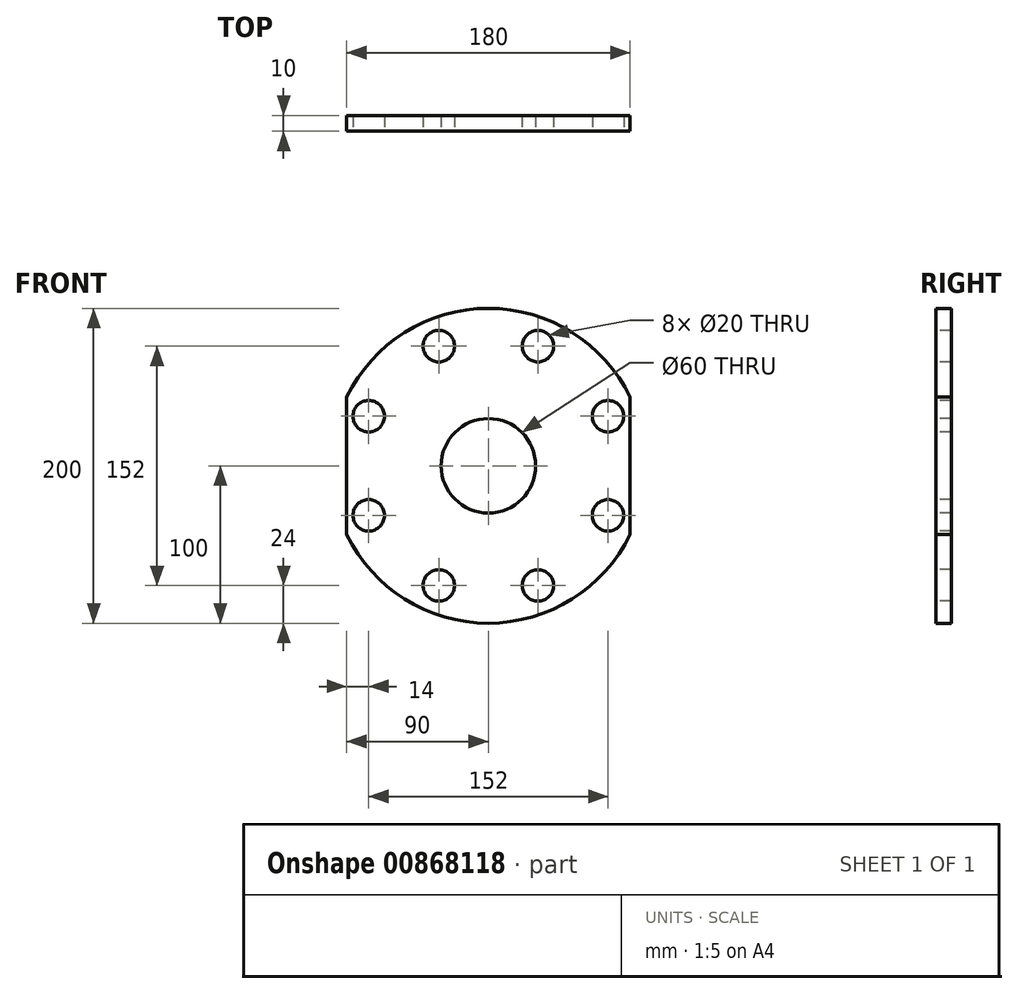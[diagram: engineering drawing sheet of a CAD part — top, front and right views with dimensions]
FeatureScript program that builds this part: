
annotation { "Feature Type Name" : "Feature", "Feature Type Description" : "" }
export const myFeature = defineFeature(function(context is Context, id is Id, definition is map)
    precondition{}
    {
        {
            var Q0;
            Q0=qCreatedBy(makeId("Front.planeOp"),FACE);
            var sketch = newSketch(context, id + "F0", { "sketchPlane" : qUnion([Q0])});
            skCircle(sketch, "E0", {"center": v(0, 0) * mm, "radius": 100 * mm});
            skSolve(sketch);
        }
        {
            var Q0;
            Q0=makeQuery(id+"F0.imprint","IMPRINT",FACE,{"disambiguationData":[TD([[makeQuery(id+"F0.imprint","IMPRINT",EDGE,{"derivedFrom":sQuery(id+"F0.wireOp",EDGE,"E0")}),1.0]])]});
            var sketch = newSketch(context, id + "F1", { "sketchPlane" : qUnion([Q0])});
            skLineSegment(sketch, "E1.bottom", {"start": v(90, 100) * mm, "end": v(-90, 100) * mm});
            skLineSegment(sketch, "E1.top", {"start": v(90, -100) * mm, "end": v(-90, -100) * mm});
            skLineSegment(sketch, "E1.left", {"start": v(90, 100) * mm, "end": v(90, -100) * mm});
            skLineSegment(sketch, "E1.right", {"start": v(-90, 100) * mm, "end": v(-90, -100) * mm});
            skPoint(sketch, "E1.middle", {"position": v(0, 0) * mm});
            skSolve(sketch);
        }
        {
            var Q0;
            Q0 = qSketchRegion(id + "F0", true);
            extrude(context, id + "F2", {"entities" : qUnion([Q0]), "depth" : 10 * mm, "offsetDistance" : 25 * mm});
        }
        {
            var Q0;
            {var subQ0=sQuery(id+"F1.wireOp",EDGE,"E1.right");var subQ1=sQuery(id+"F1.wireOp",EDGE,"E1.bottom");var subQ2=makeQuery(id+"F1.imprint","INTERSECT",VERTEX,{"derivedFrom":[subQ1,subQ0]});Q0=makeQuery(id+"F1.imprint","IMPRINT",FACE,{"disambiguationData":[TD([[makeQuery(id+"F1.imprint","IMPRINT",EDGE,{"disambiguationData":[TD([[subQ2,1.0]])],"derivedFrom":subQ1}),1.0]])]});}
            var Q1;
            {var subQ0=sQuery(id+"F1.wireOp",EDGE,"E1.right");var subQ1=makeQuery(id+"F0.imprint","IMPRINT",EDGE,{"derivedFrom":sQuery(id+"F0.wireOp",EDGE,"E0")});var subQ2=makeQuery(id+"F1.imprint","INTERSECT",VERTEX,{"disambiguationData":[OD(0.0)],"derivedFrom":[subQ1,subQ0]});Q1=makeQuery(id+"F1.imprint","IMPRINT",FACE,{"disambiguationData":[TD([[makeQuery(id+"F1.imprint","IMPRINT",EDGE,{"disambiguationData":[TD([[subQ2,-1.0]])],"derivedFrom":subQ0}),-1.0]])]});}
            var Q2;
            {var subQ0=sQuery(id+"F1.wireOp",EDGE,"E1.left");var subQ1=makeQuery(id+"F0.imprint","IMPRINT",EDGE,{"derivedFrom":sQuery(id+"F0.wireOp",EDGE,"E0")});var subQ2=makeQuery(id+"F1.imprint","INTERSECT",VERTEX,{"disambiguationData":[OD(0.0)],"derivedFrom":[subQ1,subQ0]});Q2=makeQuery(id+"F1.imprint","IMPRINT",FACE,{"disambiguationData":[TD([[makeQuery(id+"F1.imprint","IMPRINT",EDGE,{"disambiguationData":[TD([[subQ2,-1.0]])],"derivedFrom":subQ0}),1.0]])]});}
            extrude(context, id + "F3", {"entities" : qUnion([Q0, Q1, Q2]), "operationType" : NewBodyOperationType.REMOVE, "endBound" : BoundingType.THROUGH_ALL, "depth" : 25 * mm, "offsetDistance" : 25 * mm});
        }
        {
            var Q0;
            Q0=makeQuery(id+"F2.opExtrude","CAP_FACE",FACE,{"disambiguationData":[OSD([sQuery(id+"F0.wireOp",EDGE,"E0")])],"isStart":false});
            var sketch = newSketch(context, id + "F4", { "sketchPlane" : qUnion([Q0])});
            skLineSegment(sketch, "E2", {"start": v(-90, 0) * mm, "end": v(90, 0) * mm, "construction": true});
            skLineSegment(sketch, "E3", {"start": v(0, 100) * mm, "end": v(0, -100) * mm, "construction": true});
            skCircle(sketch, "E4", {"center": v(-76, 31.48) * mm, "radius": 10 * mm});
            skLineSegment(sketch, "E5", {"start": v(70.71, -70.71) * mm, "end": v(0, 0) * mm, "construction": true});
            skLineSegment(sketch, "E6", {"start": v(0, 0) * mm, "end": v(-70.71, 70.71) * mm, "construction": true});
            skLineSegment(sketch, "E7", {"start": v(0, 0) * mm, "end": v(70.71, 70.71) * mm, "construction": true});
            skLineSegment(sketch, "E8", {"start": v(0, 0) * mm, "end": v(-70.71, -70.71) * mm, "construction": true});
            skLineSegment(sketch, "E9", {"start": v(0, 0) * mm, "end": v(-90, 37.28) * mm, "construction": true});
            skCircle(sketch, "E10.1.0", {"center": v(-76, -31.48) * mm, "radius": 10 * mm});
            skCircle(sketch, "E10.2.0", {"center": v(-31.48, -76) * mm, "radius": 10 * mm});
            skCircle(sketch, "E10.3.0", {"center": v(31.48, -76) * mm, "radius": 10 * mm});
            skCircle(sketch, "E10.4.0", {"center": v(76, -31.48) * mm, "radius": 10 * mm});
            skCircle(sketch, "E10.5.0", {"center": v(76, 31.48) * mm, "radius": 10 * mm});
            skCircle(sketch, "E10.6.0", {"center": v(31.48, 76) * mm, "radius": 10 * mm});
            skCircle(sketch, "E10.7.0", {"center": v(-31.48, 76) * mm, "radius": 10 * mm});
            skPoint(sketch, "E10.center", {"position": v(0, 0) * mm});
            skSolve(sketch);
        }
        {
            var Q0;
            Q0 = qSketchRegion(id + "F4", true);
            extrude(context, id + "F5", {"entities" : qUnion([Q0]), "operationType" : NewBodyOperationType.REMOVE, "oppositeDirection" : true, "depth" : 25 * mm, "offsetDistance" : 25 * mm});
        }
        {
            var Q0;
            Q0=makeQuery(id+"F2.opExtrude","CAP_FACE",FACE,{"disambiguationData":[OSD([sQuery(id+"F0.wireOp",EDGE,"E0")])],"isStart":false});
            var sketch = newSketch(context, id + "F6", { "sketchPlane" : qUnion([Q0])});
            skCircle(sketch, "E11", {"center": v(0, 0) * mm, "radius": 30 * mm});
            skSolve(sketch);
        }
        {
            var Q0;
            Q0=makeQuery(id+"F6.imprint","IMPRINT",FACE,{"disambiguationData":[TD([[makeQuery(id+"F6.imprint","IMPRINT",EDGE,{"derivedFrom":sQuery(id+"F6.wireOp",EDGE,"E11")}),1.0]])]});
            extrude(context, id + "F7", {"entities" : qUnion([Q0]), "operationType" : NewBodyOperationType.REMOVE, "oppositeDirection" : true, "depth" : 25 * mm, "offsetDistance" : 25 * mm});
        }
    });
